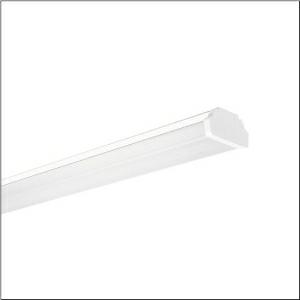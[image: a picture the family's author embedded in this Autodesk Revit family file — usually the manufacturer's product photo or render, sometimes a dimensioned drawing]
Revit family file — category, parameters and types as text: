
# Revit family: dus_r__31_gen_2_53bd812mv4a5c2_5567
name_source: partatom
category: Lighting Fixtures
units: mm (PartAtom-declared; Revit-internal decimal feet)

## family parameters
Cut with Voids When Loaded = No
Host = Face
Light Source = No
Part Type = Normal
Room Calculation Point = No
Round Connector Dimension = Use Diameter
Shared = No

## types (1)
- --- (1 x LED, 10960 lm, 60.5 W, 4000K)
    Apparent Load = 61 VA
    CIE Flux Codes = 47 80 95 93 100
    Color Rendering = 80
    Color Temperature = 4000K
    Default Elevation = 1800 mm
    Description = DUS® 31 Gen.2, luminaire insert, of sheet steel, coil coated, white, length: 1.535mm, width: 81mm, height: 90mm, 5x system unit, system units: 307mm, LED rated luminous flux: 10.960lm, light colour: 840, control gear: ON/OFF Multilumen, control gear: ECG, with plug, 3-pole, with phase selection, mains connection: 220..240V, AC, 50/60Hz, rated input power: 61W, through-wiring accessed according to module size, primary optical cover: cover, of PMMA, light emission: direct distribution, primary light characteristic: symmetric, protection rating (complete): IP20, protection rating (LED compartment): IP50, insulation class (complete): insulation class I (protective earthing), certification: CE, ENEC, VDE, UKCA, impact resistance: IK03, permissible ambient temperature for indoor applications: -35..+40°C, corresponds to IFS (International Featured Standards) requirements for safety and quality in the food industry, reducing of maximum allowable ambient temperature of 5°C with ceiling mounting, packaging unit: 1 piece
    Height = 95 mm
    Lamp = 1 x LED
    Lamp Light Flux = 10960 lm
    Lamp Power = 60.5 W
    Lamp count = 1
    Length = 1535 mm
    Luminous efficacy = 181 lm/W
    Manufacturer = Siteco
    ModVariant = No
    Model = 53BD812MV4A5C2
    Mounting Place = Ceiling
    Mounting Type = Pendant
    Number of Poles = 1
    OnlyDefault = Yes
    Power Factor = 1
    Product Name = DUS® 31 Gen.2
    Product group = luminaire insert
    ProductGroupID = 902
    Protection Class = Protection class I
    Protection Degree = IP 20
    RLX_Detail_Level = 1
    RLX_Emergency_Light_Flux = 0 lm
    RLX_Emergency_Type = 0
    RLX_Emergency_Type_DB = No
    RlxData = <blob elided: 29745 chars, md5=36e1548b>
    Socket = socket
    Standby Power = 0 W
    System Light Flux = 10960 lm
    System Power = 61 W
    Type Comments = factory setting: luminous flux: 100 % | (A | C | E) | 140 mA
    Type Image = l_1319596.jpg
    URL = http://relux.com
    VarID = @adj_042294
    Voltage = 0 V
    Weight = 0.00 kg
    Width = 81 mm

## geometry (parser evidence)
native form markers: Blend x4, Sweep x13
no freeform markers — native parametric forms only
